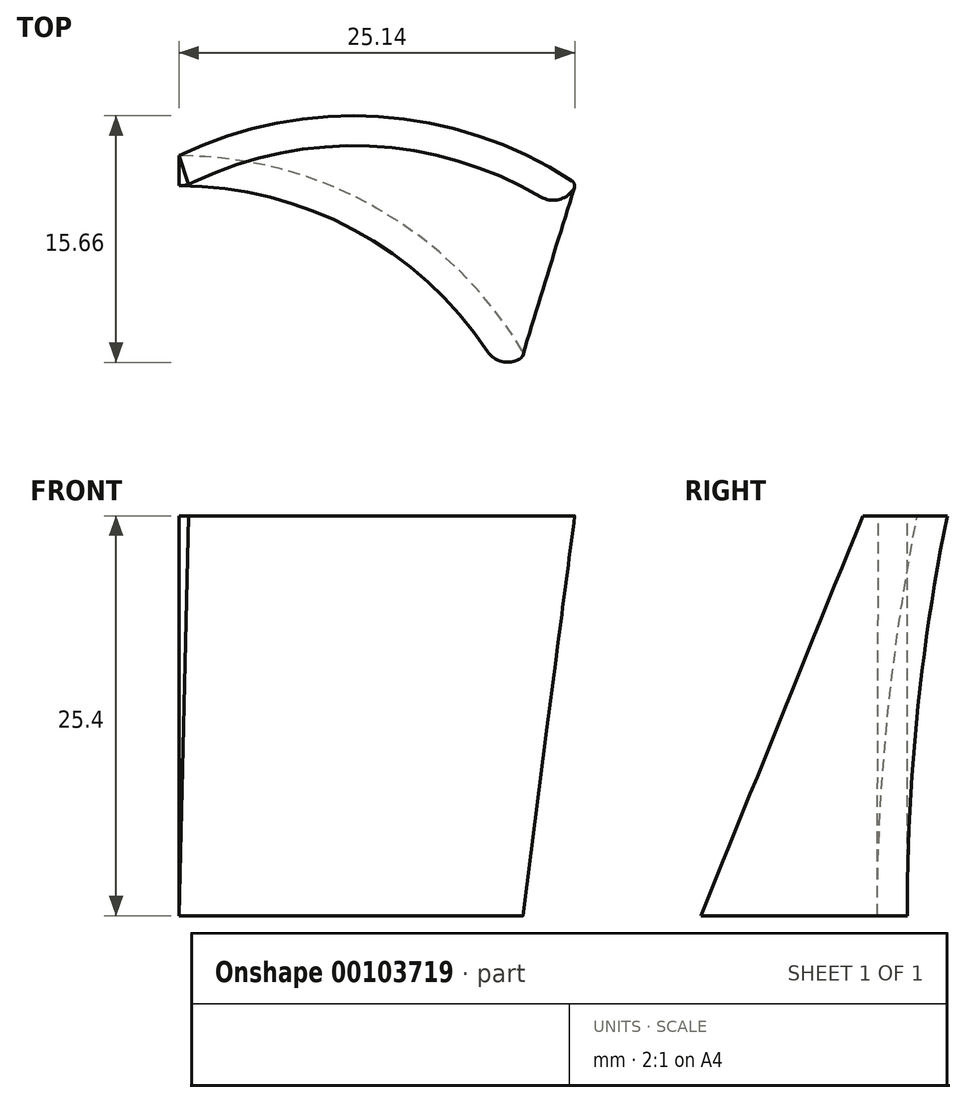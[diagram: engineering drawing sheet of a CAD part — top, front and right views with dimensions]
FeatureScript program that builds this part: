
annotation { "Feature Type Name" : "Feature", "Feature Type Description" : "" }
export const myFeature = defineFeature(function(context is Context, id is Id, definition is map)
    precondition{}
    {
        {
            var Q0;
            Q0=qCreatedBy(makeId("Top.planeOp"),FACE);
            var sketch = newSketch(context, id + "F0", { "sketchPlane" : qUnion([Q0])});
            skArc(sketch, "E0", {"start": v(21.8, -12.37) * mm, "mid": v(12.53, -3.3) * mm, "end": v(0, 0) * mm});
            skCircle(sketch, "E1", {"center": v(0, 0) * mm, "radius": 25.4 * mm});
            skArc(sketch, "E2.0", {"start": v(19.6, -12.43) * mm, "mid": v(11.12, -4.7) * mm, "end": v(0, -1.9) * mm});
            skLineSegment(sketch, "E3", {"start": v(21.63, -12.91) * mm, "end": v(21.66, -12.9) * mm});
            skLineSegment(sketch, "E4", {"start": v(0, -1.9) * mm, "end": v(0, 0) * mm});
            skPoint(sketch, "E5.visualSharp", {"position": v(20.35, -13.65) * mm});
            skArc(sketch, "E5.filletArc", {"start": v(19.6, -12.43) * mm, "mid": v(20.52, -13.08) * mm, "end": v(21.63, -12.91) * mm});
            skPoint(sketch, "E6.visualSharp", {"position": v(22, -12.7) * mm});
            skArc(sketch, "E6.filletArc", {"start": v(21.66, -12.9) * mm, "mid": v(21.84, -12.66) * mm, "end": v(21.8, -12.37) * mm});
            skSolve(sketch);
        }
        {
            var Q0;
            Q0=qCreatedBy(makeId("Top.planeOp"),FACE);
            cPlane(context, id + "F1", {"entities" : qUnion([Q0]), "cplaneType" : CPlaneType.OFFSET, "offset" : 25.4 * mm, "width" : 152.4 * mm, "height" : 152.4 * mm});
        }
        {
            var Q0;
            Q0=qCreatedBy(id+"F1.planeOp",FACE);
            var sketch = newSketch(context, id + "F2", { "sketchPlane" : qUnion([Q0])});
            skCircle(sketch, "E7", {"center": v(0, 0) * mm, "radius": 25.4 * mm});
            skArc(sketch, "E8", {"start": v(24.96, -1.6) * mm, "mid": v(12.7, 2.49) * mm, "end": v(0, 0) * mm});
            skArc(sketch, "E9.0", {"start": v(23, -2.62) * mm, "mid": v(11.9, 0.62) * mm, "end": v(0.6, -1.83) * mm});
            skLineSegment(sketch, "E10", {"start": v(24.9, -2.32) * mm, "end": v(25.04, -2.17) * mm});
            skLineSegment(sketch, "E11", {"start": v(0.6, -1.83) * mm, "end": v(0, 0) * mm});
            skPoint(sketch, "E12.visualSharp", {"position": v(24.05, -3.28) * mm});
            skArc(sketch, "E12.filletArc", {"start": v(23, -2.62) * mm, "mid": v(24, -2.8) * mm, "end": v(24.9, -2.32) * mm});
            skPoint(sketch, "E13.visualSharp", {"position": v(25.33, -1.84) * mm});
            skArc(sketch, "E13.filletArc", {"start": v(25.04, -2.17) * mm, "mid": v(25.13, -1.87) * mm, "end": v(24.96, -1.6) * mm});
            skSolve(sketch);
        }
        {
            var Q0;
            Q0=makeQuery(id+"F0.imprint","IMPRINT",FACE,{"disambiguationData":[TD([[makeQuery(id+"F0.imprint","IMPRINT",EDGE,{"derivedFrom":sQuery(id+"F0.wireOp",EDGE,"E0")}),1.0]])]});
            var Q1;
            Q1=makeQuery(id+"F2.imprint","IMPRINT",FACE,{"disambiguationData":[TD([[makeQuery(id+"F2.imprint","IMPRINT",EDGE,{"derivedFrom":sQuery(id+"F2.wireOp",EDGE,"E8")}),1.0]])]});
            loft(context, id + "F3", {"sheetProfilesArray" : [{ "sheetProfileEntities" : qUnion([Q0]) }, { "sheetProfileEntities" : qUnion([Q1]) }]});
        }
    });
